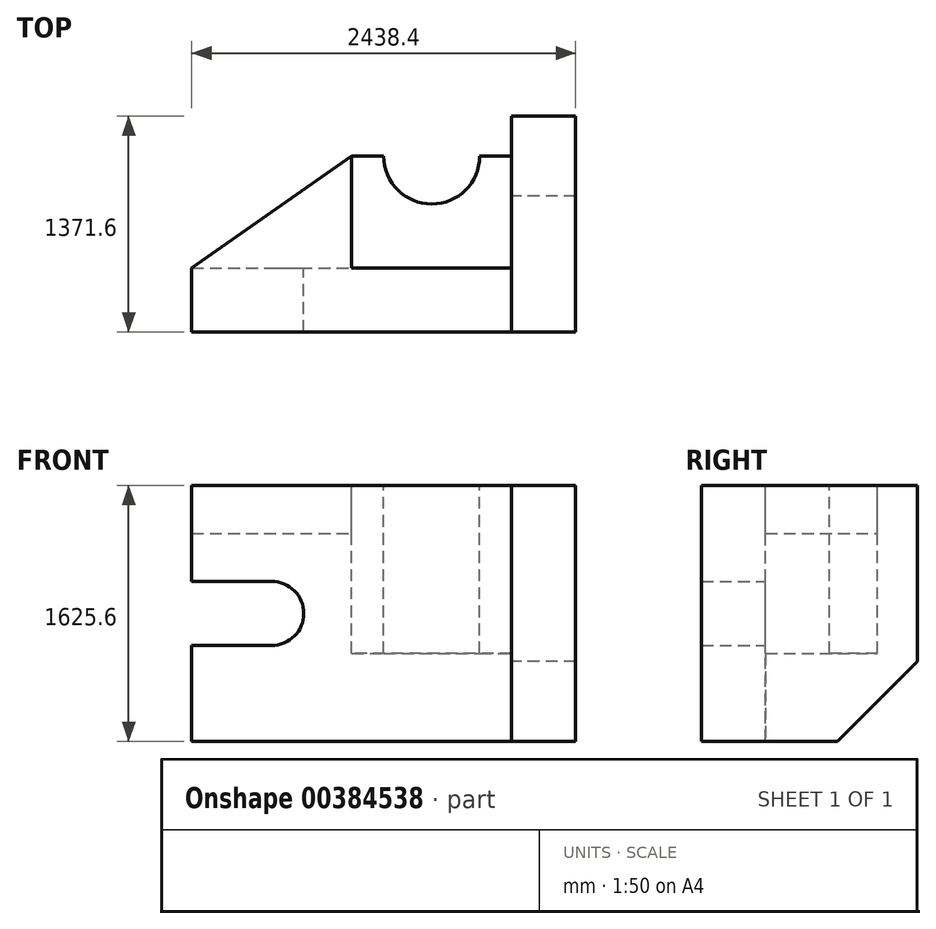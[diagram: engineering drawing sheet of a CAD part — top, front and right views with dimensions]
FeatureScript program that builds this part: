
annotation { "Feature Type Name" : "Feature", "Feature Type Description" : "" }
export const myFeature = defineFeature(function(context is Context, id is Id, definition is map)
    precondition{}
    {
        {
            var Q0;
            Q0=qCreatedBy(makeId("Front.planeOp"),FACE);
            var sketch = newSketch(context, id + "F0", { "sketchPlane" : qUnion([Q0])});
            skLineSegment(sketch, "E0", {"start": v(1977.5, 0) * mm, "end": v(-54.5, 0) * mm});
            skLineSegment(sketch, "E1", {"start": v(-54.5, 0) * mm, "end": v(-54.5, 609.6) * mm});
            skLineSegment(sketch, "E2", {"start": v(-54.5, 609.6) * mm, "end": v(453.5, 609.6) * mm});
            skLineSegment(sketch, "E3", {"start": v(453.5, 1016) * mm, "end": v(-54.5, 1016) * mm});
            skLineSegment(sketch, "E4", {"start": v(-54.5, 1016) * mm, "end": v(-54.5, 1625.6) * mm});
            skLineSegment(sketch, "E5", {"start": v(-54.5, 1625.6) * mm, "end": v(1977.5, 1625.6) * mm});
            skLineSegment(sketch, "E6", {"start": v(1977.5, 1625.6) * mm, "end": v(1977.5, 0) * mm});
            skArc(sketch, "E7", {"start": v(453.5, 609.6) * mm, "mid": v(656.7, 812.8) * mm, "end": v(453.5, 1016) * mm});
            skSolve(sketch);
        }
        {
            var Q0;
            Q0 = qSketchRegion(id + "F0", true);
            extrude(context, id + "F1", {"entities" : qUnion([Q0]), "depth" : 406.4 * mm});
        }
        {
            var Q0;
            Q0=makeQuery(id+"FvMnYx9fYLzTew7_1.boolean.opBoolean","MERGE",FACE,{"derivedFrom":[makeQuery(id+"F1.opExtrude","SWEPT_FACE",FACE,{"disambiguationData":[OSD([sQuery(id+"F0.wireOp",EDGE,"E5")])]}),makeQuery(id+"FvMnYx9fYLzTew7_1.opExtrude","SWEPT_FACE",FACE,{"disambiguationData":[OSD([sQuery(id+"FuvE6DmGQelf2DN_1.wireOp",EDGE,"QF7Cs8Ne-Z2OH-h6Fw-9tby-E8II3TbDJzo5")])]})]});
            var sketch = newSketch(context, id + "F2", { "sketchPlane" : qUnion([Q0])});
            skLineSegment(sketch, "E8", {"start": v(-54.5, 0) * mm, "end": v(961.5, 711.2) * mm});
            skLineSegment(sketch, "E9", {"start": v(961.5, 711.2) * mm, "end": v(961.5, 0) * mm});
            skLineSegment(sketch, "E10", {"start": v(961.5, 0) * mm, "end": v(-54.5, 0) * mm});
            skSolve(sketch);
        }
        {
            var Q0;
            Q0=makeQuery(id+"F2.imprint","IMPRINT",FACE,{"disambiguationData":[TD([[makeQuery(id+"F2.imprint","IMPRINT",EDGE,{"derivedFrom":sQuery(id+"F2.wireOp",EDGE,"E8")}),-1.0]])]});
            extrude(context, id + "F3", {"entities" : qUnion([Q0]), "operationType" : NewBodyOperationType.ADD, "oppositeDirection" : true, "depth" : 304.8 * mm});
        }
        {
            var Q0;
            Q0=makeQuery(id+"F1.opExtrude","SWEPT_FACE",FACE,{"disambiguationData":[OSD([sQuery(id+"F0.wireOp",EDGE,"E6")])]});
            var sketch = newSketch(context, id + "F4", { "sketchPlane" : qUnion([Q0])});
            skLineSegment(sketch, "E11", {"start": v(965.2, 1625.6) * mm, "end": v(965.2, 508) * mm});
            skLineSegment(sketch, "E12", {"start": v(457.2, 0) * mm, "end": v(965.2, 508) * mm});
            skLineSegment(sketch, "E13", {"start": v(457.2, 0) * mm, "end": v(-406.4, 0) * mm});
            skLineSegment(sketch, "E14", {"start": v(-406.4, 0) * mm, "end": v(-406.4, 1625.6) * mm});
            skLineSegment(sketch, "E15", {"start": v(-406.4, 1625.6) * mm, "end": v(965.2, 1625.6) * mm});
            skSolve(sketch);
        }
        {
            var Q0;
            Q0=makeQuery(id+"F3.boolean.opBoolean","MERGE",FACE,{"derivedFrom":[makeQuery(id+"FvMnYx9fYLzTew7_1.boolean.opBoolean","MERGE",FACE,{"derivedFrom":[makeQuery(id+"F1.opExtrude","SWEPT_FACE",FACE,{"disambiguationData":[OSD([sQuery(id+"F0.wireOp",EDGE,"E5")])]}),makeQuery(id+"FvMnYx9fYLzTew7_1.opExtrude","SWEPT_FACE",FACE,{"disambiguationData":[OSD([sQuery(id+"FuvE6DmGQelf2DN_1.wireOp",EDGE,"QF7Cs8Ne-Z2OH-h6Fw-9tby-E8II3TbDJzo5")])]})]}),makeQuery(id+"F3.opExtrude","CAP_FACE",FACE,{"disambiguationData":[OSD([sQuery(id+"F2.wireOp",EDGE,"E8"),sQuery(id+"F2.wireOp",EDGE,"E9"),sQuery(id+"F2.wireOp",EDGE,"E10")])],"isStart":true})]});
            var sketch = newSketch(context, id + "F5", { "sketchPlane" : qUnion([Q0])});
            skLineSegment(sketch, "E16", {"start": v(961.5, 711.2) * mm, "end": v(1164.7, 711.2) * mm});
            skLineSegment(sketch, "E17", {"start": v(1977.5, 711.2) * mm, "end": v(1977.5, 0) * mm});
            skLineSegment(sketch, "E18", {"start": v(1977.5, 0) * mm, "end": v(961.5, 0) * mm});
            skLineSegment(sketch, "E19", {"start": v(961.5, 0) * mm, "end": v(961.5, 711.2) * mm});
            skArc(sketch, "E20", {"start": v(1164.7, 711.2) * mm, "mid": v(1469.5, 406.4) * mm, "end": v(1774.3, 711.2) * mm});
            skLineSegment(sketch, "E21.trimOffspring", {"start": v(1774.3, 711.2) * mm, "end": v(1977.5, 711.2) * mm});
            skSolve(sketch);
        }
        {
            var Q0;
            Q0=makeQuery(id+"F5.imprint","IMPRINT",FACE,{"disambiguationData":[TD([[makeQuery(id+"F5.imprint","IMPRINT",EDGE,{"derivedFrom":sQuery(id+"F5.wireOp",EDGE,"E16")}),-1.0]])]});
            extrude(context, id + "F6", {"entities" : qUnion([Q0]), "oppositeDirection" : true, "depth" : 1066.8 * mm});
        }
        {
            var Q0;
            Q0 = qSketchRegion(id + "F4", true);
            extrude(context, id + "F7", {"entities" : qUnion([Q0]), "depth" : 406.4 * mm});
        }
    });
